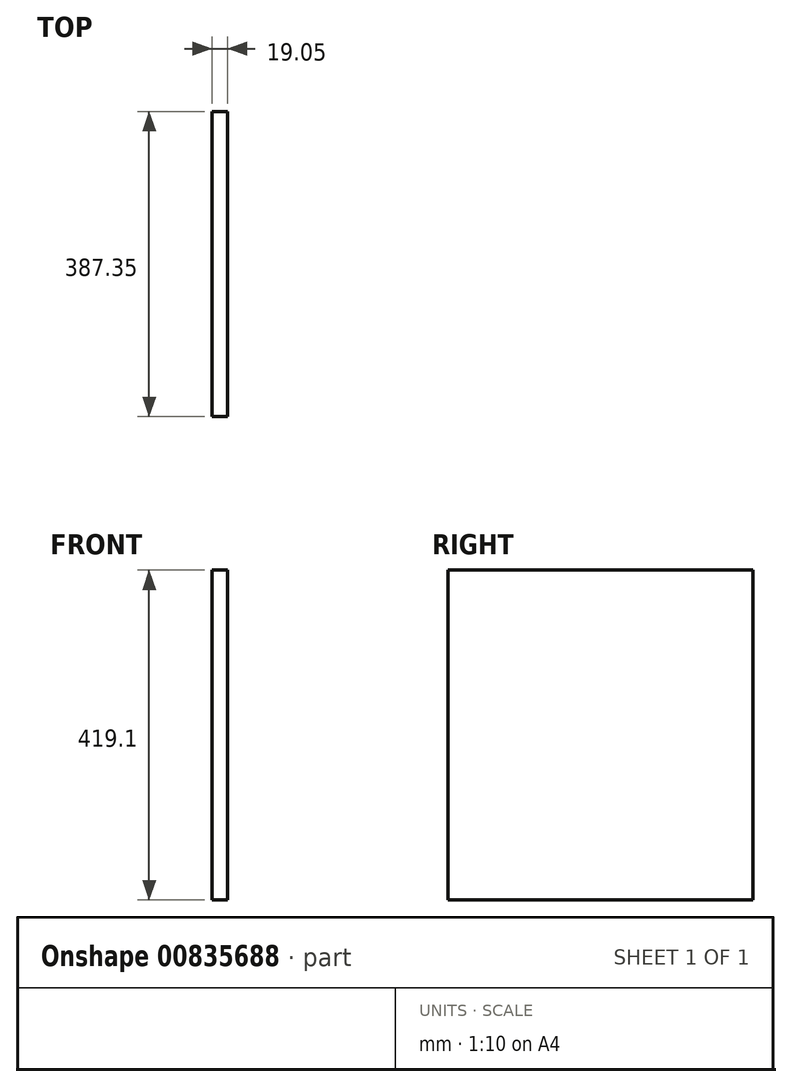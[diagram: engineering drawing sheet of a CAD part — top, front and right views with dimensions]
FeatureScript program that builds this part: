
annotation { "Feature Type Name" : "Feature", "Feature Type Description" : "" }
export const myFeature = defineFeature(function(context is Context, id is Id, definition is map)
    precondition{}
    {
        {
            var Q0;
            Q0=qCreatedBy(makeId("Right.planeOp"),FACE);
            var sketch = newSketch(context, id + "F0", { "sketchPlane" : qUnion([Q0])});
            skLineSegment(sketch, "E0.bottom", {"start": v(0, 0) * mm, "end": v(387.35, 0) * mm});
            skLineSegment(sketch, "E0.top", {"start": v(0, 419.1) * mm, "end": v(387.35, 419.1) * mm});
            skLineSegment(sketch, "E0.left", {"start": v(0, 0) * mm, "end": v(0, 419.1) * mm});
            skLineSegment(sketch, "E0.right", {"start": v(387.35, 0) * mm, "end": v(387.35, 419.1) * mm});
            skSolve(sketch);
        }
        {
            var Q0;
            Q0 = qSketchRegion(id + "F0", true);
            extrude(context, id + "F1", {"entities" : qUnion([Q0]), "depth" : 19.05 * mm, "offsetDistance" : 25.4 * mm});
        }
    });
